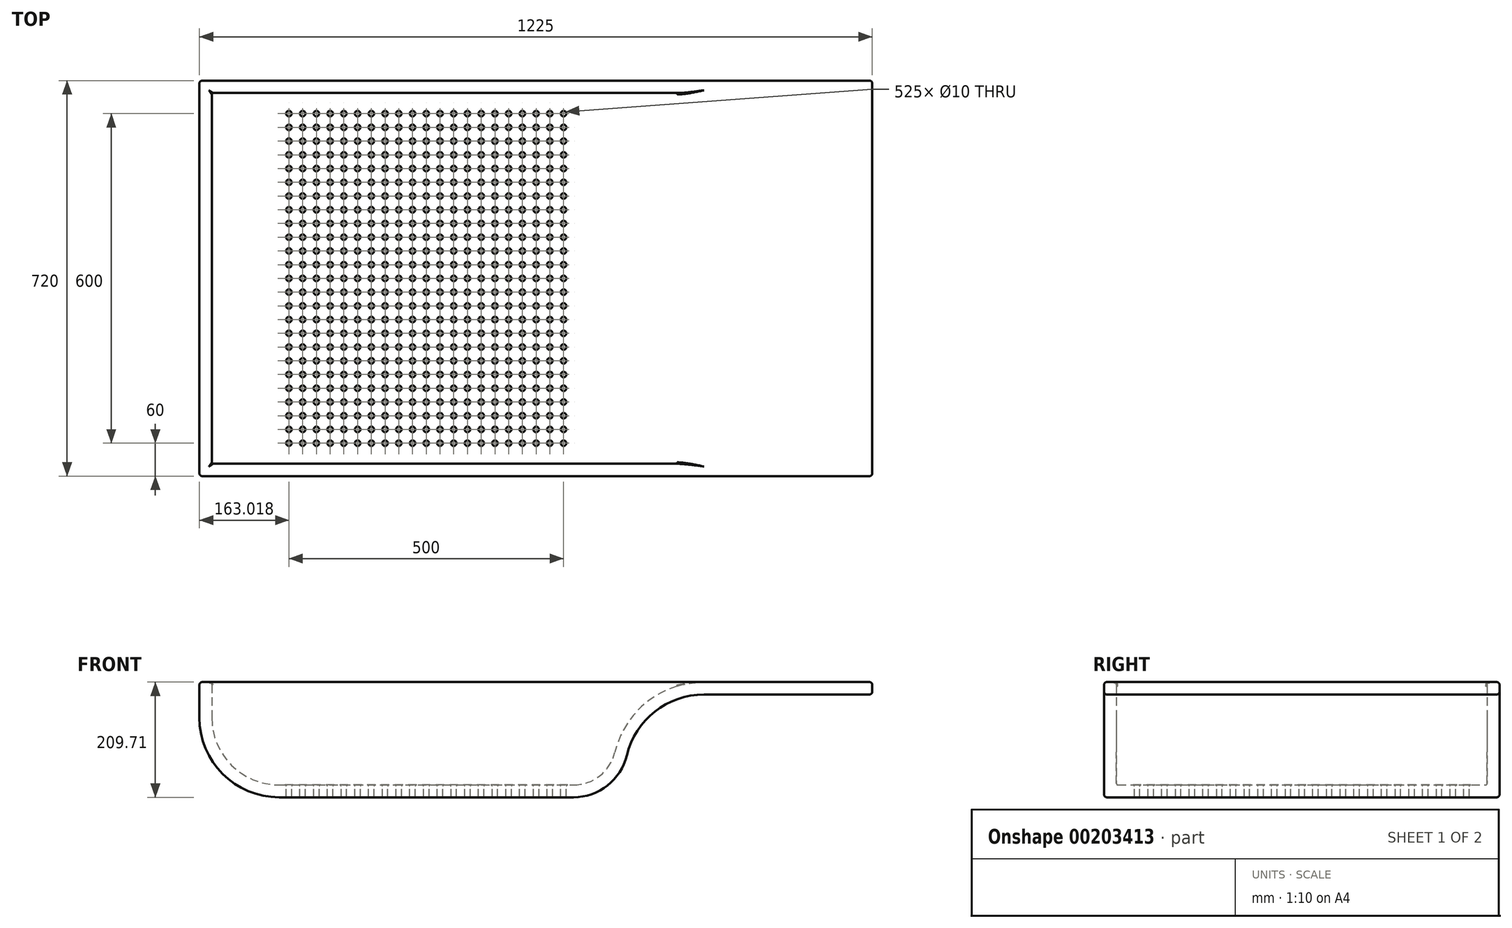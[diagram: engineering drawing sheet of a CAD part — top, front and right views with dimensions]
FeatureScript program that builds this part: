
annotation { "Feature Type Name" : "Feature", "Feature Type Description" : "" }
export const myFeature = defineFeature(function(context is Context, id is Id, definition is map)
    precondition{}
    {
        {
            var Q0;
            Q0=qCreatedBy(makeId("Front.planeOp"),FACE);
            var sketch = newSketch(context, id + "F0", { "sketchPlane" : qUnion([Q0])});
            skLineSegment(sketch, "E0.bottom", {"start": v(-612.5, 108.01) * mm, "end": v(612.5, 108.01) * mm});
            skLineSegment(sketch, "E0.top", {"start": v(-467.5, -101.7) * mm, "end": v(68.54, -101.7) * mm});
            skLineSegment(sketch, "E0.left", {"start": v(-612.5, 108.01) * mm, "end": v(-612.5, 43.3) * mm});
            skPoint(sketch, "E0.middle", {"position": v(0, 0) * mm});
            skPoint(sketch, "E1", {"position": v(207.5, -101.7) * mm});
            skPoint(sketch, "E2", {"position": v(207.5, 108.01) * mm});
            skPoint(sketch, "E3", {"position": v(612.5, 85.51) * mm});
            skLineSegment(sketch, "E4", {"start": v(306.28, 85.51) * mm, "end": v(612.5, 85.51) * mm});
            skArc(sketch, "E5.filletArc", {"start": v(-612.5, 43.3) * mm, "mid": v(-570.03, -59.23) * mm, "end": v(-467.5, -101.7) * mm});
            skArc(sketch, "E6", {"start": v(306.28, 85.51) * mm, "mid": v(216.84, 54.53) * mm, "end": v(165.75, -25.15) * mm});
            skArc(sketch, "E7.filletArc", {"start": v(68.54, -101.7) * mm, "mid": v(130.4, -80.27) * mm, "end": v(165.75, -25.15) * mm});
            skLineSegment(sketch, "E8", {"start": v(612.5, 108.01) * mm, "end": v(612.5, 85.51) * mm});
            skPoint(sketch, "E9", {"position": v(308.18, 108.01) * mm});
            skSolve(sketch);
        }
        {
            var Q0;
            Q0=qSketchRegion(id+"F0",true);
            extrude(context, id + "F1", {"entities" : qUnion([Q0]), "depth" : 360 * mm, "hasSecondDirection" : true, "secondDirectionOppositeDirection" : true, "secondDirectionDepth" : 360 * mm});
        }
        {
            var Q0;
            Q0=makeQuery(id+"F1.opExtrude","SWEPT_FACE",FACE,{"disambiguationData":[OSD([sQuery(id+"F0.wireOp",EDGE,"E0.bottom")])]});
            shell(context, id + "F2", {"entities" : qUnion([Q0]), "thickness" : 22.5 * mm});
        }
        {
            var Q0;
            Q0=makeQuery(id+"F1.opExtrude","CAP_EDGE",EDGE,{"disambiguationData":[OSD([sQuery(id+"F0.wireOp",EDGE,"E0.bottom")])],"isStart":false});
            var Q1;
            Q1=makeQuery(id+"F1.opExtrude","CAP_EDGE",EDGE,{"disambiguationData":[OSD([sQuery(id+"F0.wireOp",EDGE,"E8")])],"isStart":false});
            var Q2;
            Q2=makeQuery(id+"F1.opExtrude","SWEPT_EDGE",EDGE,{"disambiguationData":[OSD([sQuery(id+"F0.wireOp",EDGE,"E0.bottom"),sQuery(id+"F0.wireOp",EDGE,"E8")])]});
            var Q3;
            Q3=makeQuery(id+"F1.opExtrude","SWEPT_EDGE",EDGE,{"disambiguationData":[OSD([sQuery(id+"F0.wireOp",EDGE,"E4"),sQuery(id+"F0.wireOp",EDGE,"E8")])]});
            var Q4;
            Q4=makeQuery(id+"F1.opExtrude","CAP_EDGE",EDGE,{"disambiguationData":[OSD([sQuery(id+"F0.wireOp",EDGE,"E8")])],"isStart":true});
            var Q5;
            Q5=makeQuery(id+"F1.opExtrude","CAP_EDGE",EDGE,{"disambiguationData":[OSD([sQuery(id+"F0.wireOp",EDGE,"E4")])],"isStart":true});
            var Q6;
            Q6=makeQuery(id+"F1.opExtrude","CAP_EDGE",EDGE,{"disambiguationData":[OSD([sQuery(id+"F0.wireOp",EDGE,"E0.bottom")])],"isStart":true});
            var Q7;
            {var subQ0=sQuery(id+"F0.wireOp",EDGE,"E0.bottom");Q7=makeQuery(id+"F2.opShell","OFFSET_EDGE",EDGE,{"disambiguationData":[OSD([subQ0]),TDD([makeQuery(id+"F1.opExtrude","CAP_EDGE",EDGE,{"disambiguationData":[OSD([subQ0])],"isStart":true})])]});}
            var Q8;
            {var subQ0=sQuery(id+"F0.wireOp",EDGE,"E0.bottom");Q8=makeQuery(id+"F2.opShell","OFFSET_EDGE",EDGE,{"disambiguationData":[OSD([subQ0]),TDD([makeQuery(id+"F1.opExtrude","CAP_EDGE",EDGE,{"disambiguationData":[OSD([subQ0])],"isStart":false})])]});}
            var Q9;
            Q9=makeQuery(id+"F1.opExtrude","CAP_EDGE",EDGE,{"disambiguationData":[OSD([sQuery(id+"F0.wireOp",EDGE,"E6")])],"isStart":false});
            var Q10;
            Q10=makeQuery(id+"F2.opShell","OFFSET_EDGE",EDGE,{"disambiguationData":[OSD([sQuery(id+"F0.wireOp",EDGE,"E0.bottom"),sQuery(id+"F0.wireOp",EDGE,"E0.left")])]});
            var Q11;
            Q11=makeQuery(id+"F1.opExtrude","SWEPT_EDGE",EDGE,{"disambiguationData":[OSD([sQuery(id+"F0.wireOp",EDGE,"E0.bottom"),sQuery(id+"F0.wireOp",EDGE,"E0.left")])]});
            fillet(context, id + "F3", {"entities" : qUnion([Q0, Q1, Q2, Q3, Q4, Q5, Q6, Q7, Q8, Q9, Q10, Q11]), "radius" : 5 * mm, "tangentPropagation" : true, "allowEdgeOverflow" : false});
        }
        {
            var Q0;
            Q0=makeQuery(id+"F2.opShell","OFFSET_FACE",FACE,{"disambiguationData":[OSD([sQuery(id+"F0.wireOp",EDGE,"E0.top")])]});
            var sketch = newSketch(context, id + "F4", { "sketchPlane" : qUnion([Q0])});
            skCircle(sketch, "E10", {"center": v(-199.48, 0) * mm, "radius": 5 * mm});
            skPoint(sketch, "E10.centerSnap0", {"position": v(-199.48, 337.5) * mm});
            skCircle(sketch, "E11.0.1.0", {"center": v(-199.48, 25) * mm, "radius": 5 * mm});
            skCircle(sketch, "E11.0.2.0", {"center": v(-199.48, 50) * mm, "radius": 5 * mm});
            skCircle(sketch, "E11.0.3.0", {"center": v(-199.48, 75) * mm, "radius": 5 * mm});
            skCircle(sketch, "E11.0.4.0", {"center": v(-199.48, 100) * mm, "radius": 5 * mm});
            skCircle(sketch, "E11.0.5.0", {"center": v(-199.48, 125) * mm, "radius": 5 * mm});
            skCircle(sketch, "E11.0.6.0", {"center": v(-199.48, 150) * mm, "radius": 5 * mm});
            skCircle(sketch, "E11.0.7.0", {"center": v(-199.48, 175) * mm, "radius": 5 * mm});
            skCircle(sketch, "E11.0.8.0", {"center": v(-199.48, 200) * mm, "radius": 5 * mm});
            skCircle(sketch, "E11.0.9.0", {"center": v(-199.48, 225) * mm, "radius": 5 * mm});
            skCircle(sketch, "E11.0.10.0", {"center": v(-199.48, 250) * mm, "radius": 5 * mm});
            skCircle(sketch, "E11.0.11.0", {"center": v(-199.48, 275) * mm, "radius": 5 * mm});
            skCircle(sketch, "E11.0.12.0", {"center": v(-199.48, 300) * mm, "radius": 5 * mm});
            skCircle(sketch, "E11.1.0.0", {"center": v(-174.48, 0) * mm, "radius": 5 * mm});
            skCircle(sketch, "E11.1.1.0", {"center": v(-174.48, 25) * mm, "radius": 5 * mm});
            skCircle(sketch, "E11.1.2.0", {"center": v(-174.48, 50) * mm, "radius": 5 * mm});
            skCircle(sketch, "E11.1.3.0", {"center": v(-174.48, 75) * mm, "radius": 5 * mm});
            skCircle(sketch, "E11.1.4.0", {"center": v(-174.48, 100) * mm, "radius": 5 * mm});
            skCircle(sketch, "E11.1.5.0", {"center": v(-174.48, 125) * mm, "radius": 5 * mm});
            skCircle(sketch, "E11.1.6.0", {"center": v(-174.48, 150) * mm, "radius": 5 * mm});
            skCircle(sketch, "E11.1.7.0", {"center": v(-174.48, 175) * mm, "radius": 5 * mm});
            skCircle(sketch, "E11.1.8.0", {"center": v(-174.48, 200) * mm, "radius": 5 * mm});
            skCircle(sketch, "E11.1.9.0", {"center": v(-174.48, 225) * mm, "radius": 5 * mm});
            skCircle(sketch, "E11.1.10.0", {"center": v(-174.48, 250) * mm, "radius": 5 * mm});
            skCircle(sketch, "E11.1.11.0", {"center": v(-174.48, 275) * mm, "radius": 5 * mm});
            skCircle(sketch, "E11.1.12.0", {"center": v(-174.48, 300) * mm, "radius": 5 * mm});
            skCircle(sketch, "E11.2.0.0", {"center": v(-149.48, 0) * mm, "radius": 5 * mm});
            skCircle(sketch, "E11.2.1.0", {"center": v(-149.48, 25) * mm, "radius": 5 * mm});
            skCircle(sketch, "E11.2.2.0", {"center": v(-149.48, 50) * mm, "radius": 5 * mm});
            skCircle(sketch, "E11.2.3.0", {"center": v(-149.48, 75) * mm, "radius": 5 * mm});
            skCircle(sketch, "E11.2.4.0", {"center": v(-149.48, 100) * mm, "radius": 5 * mm});
            skCircle(sketch, "E11.2.5.0", {"center": v(-149.48, 125) * mm, "radius": 5 * mm});
            skCircle(sketch, "E11.2.6.0", {"center": v(-149.48, 150) * mm, "radius": 5 * mm});
            skCircle(sketch, "E11.2.7.0", {"center": v(-149.48, 175) * mm, "radius": 5 * mm});
            skCircle(sketch, "E11.2.8.0", {"center": v(-149.48, 200) * mm, "radius": 5 * mm});
            skCircle(sketch, "E11.2.9.0", {"center": v(-149.48, 225) * mm, "radius": 5 * mm});
            skCircle(sketch, "E11.2.10.0", {"center": v(-149.48, 250) * mm, "radius": 5 * mm});
            skCircle(sketch, "E11.2.11.0", {"center": v(-149.48, 275) * mm, "radius": 5 * mm});
            skCircle(sketch, "E11.2.12.0", {"center": v(-149.48, 300) * mm, "radius": 5 * mm});
            skCircle(sketch, "E11.3.0.0", {"center": v(-124.48, 0) * mm, "radius": 5 * mm});
            skCircle(sketch, "E11.3.1.0", {"center": v(-124.48, 25) * mm, "radius": 5 * mm});
            skCircle(sketch, "E11.3.2.0", {"center": v(-124.48, 50) * mm, "radius": 5 * mm});
            skCircle(sketch, "E11.3.3.0", {"center": v(-124.48, 75) * mm, "radius": 5 * mm});
            skCircle(sketch, "E11.3.4.0", {"center": v(-124.48, 100) * mm, "radius": 5 * mm});
            skCircle(sketch, "E11.3.5.0", {"center": v(-124.48, 125) * mm, "radius": 5 * mm});
            skCircle(sketch, "E11.3.6.0", {"center": v(-124.48, 150) * mm, "radius": 5 * mm});
            skCircle(sketch, "E11.3.7.0", {"center": v(-124.48, 175) * mm, "radius": 5 * mm});
            skCircle(sketch, "E11.3.8.0", {"center": v(-124.48, 200) * mm, "radius": 5 * mm});
            skCircle(sketch, "E11.3.9.0", {"center": v(-124.48, 225) * mm, "radius": 5 * mm});
            skCircle(sketch, "E11.3.10.0", {"center": v(-124.48, 250) * mm, "radius": 5 * mm});
            skCircle(sketch, "E11.3.11.0", {"center": v(-124.48, 275) * mm, "radius": 5 * mm});
            skCircle(sketch, "E11.3.12.0", {"center": v(-124.48, 300) * mm, "radius": 5 * mm});
            skCircle(sketch, "E11.4.0.0", {"center": v(-99.48, 0) * mm, "radius": 5 * mm});
            skCircle(sketch, "E11.4.1.0", {"center": v(-99.48, 25) * mm, "radius": 5 * mm});
            skCircle(sketch, "E11.4.2.0", {"center": v(-99.48, 50) * mm, "radius": 5 * mm});
            skCircle(sketch, "E11.4.3.0", {"center": v(-99.48, 75) * mm, "radius": 5 * mm});
            skCircle(sketch, "E11.4.4.0", {"center": v(-99.48, 100) * mm, "radius": 5 * mm});
            skCircle(sketch, "E11.4.5.0", {"center": v(-99.48, 125) * mm, "radius": 5 * mm});
            skCircle(sketch, "E11.4.6.0", {"center": v(-99.48, 150) * mm, "radius": 5 * mm});
            skCircle(sketch, "E11.4.7.0", {"center": v(-99.48, 175) * mm, "radius": 5 * mm});
            skCircle(sketch, "E11.4.8.0", {"center": v(-99.48, 200) * mm, "radius": 5 * mm});
            skCircle(sketch, "E11.4.9.0", {"center": v(-99.48, 225) * mm, "radius": 5 * mm});
            skCircle(sketch, "E11.4.10.0", {"center": v(-99.48, 250) * mm, "radius": 5 * mm});
            skCircle(sketch, "E11.4.11.0", {"center": v(-99.48, 275) * mm, "radius": 5 * mm});
            skCircle(sketch, "E11.4.12.0", {"center": v(-99.48, 300) * mm, "radius": 5 * mm});
            skCircle(sketch, "E11.5.0.0", {"center": v(-74.48, 0) * mm, "radius": 5 * mm});
            skCircle(sketch, "E11.5.1.0", {"center": v(-74.48, 25) * mm, "radius": 5 * mm});
            skCircle(sketch, "E11.5.2.0", {"center": v(-74.48, 50) * mm, "radius": 5 * mm});
            skCircle(sketch, "E11.5.3.0", {"center": v(-74.48, 75) * mm, "radius": 5 * mm});
            skCircle(sketch, "E11.5.4.0", {"center": v(-74.48, 100) * mm, "radius": 5 * mm});
            skCircle(sketch, "E11.5.5.0", {"center": v(-74.48, 125) * mm, "radius": 5 * mm});
            skCircle(sketch, "E11.5.6.0", {"center": v(-74.48, 150) * mm, "radius": 5 * mm});
            skCircle(sketch, "E11.5.7.0", {"center": v(-74.48, 175) * mm, "radius": 5 * mm});
            skCircle(sketch, "E11.5.8.0", {"center": v(-74.48, 200) * mm, "radius": 5 * mm});
            skCircle(sketch, "E11.5.9.0", {"center": v(-74.48, 225) * mm, "radius": 5 * mm});
            skCircle(sketch, "E11.5.10.0", {"center": v(-74.48, 250) * mm, "radius": 5 * mm});
            skCircle(sketch, "E11.5.11.0", {"center": v(-74.48, 275) * mm, "radius": 5 * mm});
            skCircle(sketch, "E11.5.12.0", {"center": v(-74.48, 300) * mm, "radius": 5 * mm});
            skCircle(sketch, "E11.6.0.0", {"center": v(-49.48, 0) * mm, "radius": 5 * mm});
            skCircle(sketch, "E11.6.1.0", {"center": v(-49.48, 25) * mm, "radius": 5 * mm});
            skCircle(sketch, "E11.6.2.0", {"center": v(-49.48, 50) * mm, "radius": 5 * mm});
            skCircle(sketch, "E11.6.3.0", {"center": v(-49.48, 75) * mm, "radius": 5 * mm});
            skCircle(sketch, "E11.6.4.0", {"center": v(-49.48, 100) * mm, "radius": 5 * mm});
            skCircle(sketch, "E11.6.5.0", {"center": v(-49.48, 125) * mm, "radius": 5 * mm});
            skCircle(sketch, "E11.6.6.0", {"center": v(-49.48, 150) * mm, "radius": 5 * mm});
            skCircle(sketch, "E11.6.7.0", {"center": v(-49.48, 175) * mm, "radius": 5 * mm});
            skCircle(sketch, "E11.6.8.0", {"center": v(-49.48, 200) * mm, "radius": 5 * mm});
            skCircle(sketch, "E11.6.9.0", {"center": v(-49.48, 225) * mm, "radius": 5 * mm});
            skCircle(sketch, "E11.6.10.0", {"center": v(-49.48, 250) * mm, "radius": 5 * mm});
            skCircle(sketch, "E11.6.11.0", {"center": v(-49.48, 275) * mm, "radius": 5 * mm});
            skCircle(sketch, "E11.6.12.0", {"center": v(-49.48, 300) * mm, "radius": 5 * mm});
            skCircle(sketch, "E11.7.0.0", {"center": v(-24.48, 0) * mm, "radius": 5 * mm});
            skCircle(sketch, "E11.7.1.0", {"center": v(-24.48, 25) * mm, "radius": 5 * mm});
            skCircle(sketch, "E11.7.2.0", {"center": v(-24.48, 50) * mm, "radius": 5 * mm});
            skCircle(sketch, "E11.7.3.0", {"center": v(-24.48, 75) * mm, "radius": 5 * mm});
            skCircle(sketch, "E11.7.4.0", {"center": v(-24.48, 100) * mm, "radius": 5 * mm});
            skCircle(sketch, "E11.7.5.0", {"center": v(-24.48, 125) * mm, "radius": 5 * mm});
            skCircle(sketch, "E11.7.6.0", {"center": v(-24.48, 150) * mm, "radius": 5 * mm});
            skCircle(sketch, "E11.7.7.0", {"center": v(-24.48, 175) * mm, "radius": 5 * mm});
            skCircle(sketch, "E11.7.8.0", {"center": v(-24.48, 200) * mm, "radius": 5 * mm});
            skCircle(sketch, "E11.7.9.0", {"center": v(-24.48, 225) * mm, "radius": 5 * mm});
            skCircle(sketch, "E11.7.10.0", {"center": v(-24.48, 250) * mm, "radius": 5 * mm});
            skCircle(sketch, "E11.7.11.0", {"center": v(-24.48, 275) * mm, "radius": 5 * mm});
            skCircle(sketch, "E11.7.12.0", {"center": v(-24.48, 300) * mm, "radius": 5 * mm});
            skCircle(sketch, "E11.8.0.0", {"center": v(0.52, 0) * mm, "radius": 5 * mm});
            skCircle(sketch, "E11.8.1.0", {"center": v(0.52, 25) * mm, "radius": 5 * mm});
            skCircle(sketch, "E11.8.2.0", {"center": v(0.52, 50) * mm, "radius": 5 * mm});
            skCircle(sketch, "E11.8.3.0", {"center": v(0.52, 75) * mm, "radius": 5 * mm});
            skCircle(sketch, "E11.8.4.0", {"center": v(0.52, 100) * mm, "radius": 5 * mm});
            skCircle(sketch, "E11.8.5.0", {"center": v(0.52, 125) * mm, "radius": 5 * mm});
            skCircle(sketch, "E11.8.6.0", {"center": v(0.52, 150) * mm, "radius": 5 * mm});
            skCircle(sketch, "E11.8.7.0", {"center": v(0.52, 175) * mm, "radius": 5 * mm});
            skCircle(sketch, "E11.8.8.0", {"center": v(0.52, 200) * mm, "radius": 5 * mm});
            skCircle(sketch, "E11.8.9.0", {"center": v(0.52, 225) * mm, "radius": 5 * mm});
            skCircle(sketch, "E11.8.10.0", {"center": v(0.52, 250) * mm, "radius": 5 * mm});
            skCircle(sketch, "E11.8.11.0", {"center": v(0.52, 275) * mm, "radius": 5 * mm});
            skCircle(sketch, "E11.8.12.0", {"center": v(0.52, 300) * mm, "radius": 5 * mm});
            skCircle(sketch, "E11.9.0.0", {"center": v(25.52, 0) * mm, "radius": 5 * mm});
            skCircle(sketch, "E11.9.1.0", {"center": v(25.52, 25) * mm, "radius": 5 * mm});
            skCircle(sketch, "E11.9.2.0", {"center": v(25.52, 50) * mm, "radius": 5 * mm});
            skCircle(sketch, "E11.9.3.0", {"center": v(25.52, 75) * mm, "radius": 5 * mm});
            skCircle(sketch, "E11.9.4.0", {"center": v(25.52, 100) * mm, "radius": 5 * mm});
            skCircle(sketch, "E11.9.5.0", {"center": v(25.52, 125) * mm, "radius": 5 * mm});
            skCircle(sketch, "E11.9.6.0", {"center": v(25.52, 150) * mm, "radius": 5 * mm});
            skCircle(sketch, "E11.9.7.0", {"center": v(25.52, 175) * mm, "radius": 5 * mm});
            skCircle(sketch, "E11.9.8.0", {"center": v(25.52, 200) * mm, "radius": 5 * mm});
            skCircle(sketch, "E11.9.9.0", {"center": v(25.52, 225) * mm, "radius": 5 * mm});
            skCircle(sketch, "E11.9.10.0", {"center": v(25.52, 250) * mm, "radius": 5 * mm});
            skCircle(sketch, "E11.9.11.0", {"center": v(25.52, 275) * mm, "radius": 5 * mm});
            skCircle(sketch, "E11.9.12.0", {"center": v(25.52, 300) * mm, "radius": 5 * mm});
            skCircle(sketch, "E11.10.0.0", {"center": v(50.52, 0) * mm, "radius": 5 * mm});
            skCircle(sketch, "E11.10.1.0", {"center": v(50.52, 25) * mm, "radius": 5 * mm});
            skCircle(sketch, "E11.10.2.0", {"center": v(50.52, 50) * mm, "radius": 5 * mm});
            skCircle(sketch, "E11.10.3.0", {"center": v(50.52, 75) * mm, "radius": 5 * mm});
            skCircle(sketch, "E11.10.4.0", {"center": v(50.52, 100) * mm, "radius": 5 * mm});
            skCircle(sketch, "E11.10.5.0", {"center": v(50.52, 125) * mm, "radius": 5 * mm});
            skCircle(sketch, "E11.10.6.0", {"center": v(50.52, 150) * mm, "radius": 5 * mm});
            skCircle(sketch, "E11.10.7.0", {"center": v(50.52, 175) * mm, "radius": 5 * mm});
            skCircle(sketch, "E11.10.8.0", {"center": v(50.52, 200) * mm, "radius": 5 * mm});
            skCircle(sketch, "E11.10.9.0", {"center": v(50.52, 225) * mm, "radius": 5 * mm});
            skCircle(sketch, "E11.10.10.0", {"center": v(50.52, 250) * mm, "radius": 5 * mm});
            skCircle(sketch, "E11.10.11.0", {"center": v(50.52, 275) * mm, "radius": 5 * mm});
            skCircle(sketch, "E11.10.12.0", {"center": v(50.52, 300) * mm, "radius": 5 * mm});
            skCircle(sketch, "E12.0.1.0", {"center": v(-199.48, -25) * mm, "radius": 5 * mm});
            skCircle(sketch, "E12.0.2.0", {"center": v(-199.48, -50) * mm, "radius": 5 * mm});
            skCircle(sketch, "E12.0.3.0", {"center": v(-199.48, -75) * mm, "radius": 5 * mm});
            skCircle(sketch, "E12.0.4.0", {"center": v(-199.48, -100) * mm, "radius": 5 * mm});
            skCircle(sketch, "E12.0.5.0", {"center": v(-199.48, -125) * mm, "radius": 5 * mm});
            skCircle(sketch, "E12.0.6.0", {"center": v(-199.48, -150) * mm, "radius": 5 * mm});
            skCircle(sketch, "E12.0.7.0", {"center": v(-199.48, -175) * mm, "radius": 5 * mm});
            skCircle(sketch, "E12.0.8.0", {"center": v(-199.48, -200) * mm, "radius": 5 * mm});
            skCircle(sketch, "E12.0.9.0", {"center": v(-199.48, -225) * mm, "radius": 5 * mm});
            skCircle(sketch, "E12.0.10.0", {"center": v(-199.48, -250) * mm, "radius": 5 * mm});
            skCircle(sketch, "E12.0.11.0", {"center": v(-199.48, -275) * mm, "radius": 5 * mm});
            skCircle(sketch, "E12.0.12.0", {"center": v(-199.48, -300) * mm, "radius": 5 * mm});
            skCircle(sketch, "E12.1.1.0", {"center": v(-174.48, -25) * mm, "radius": 5 * mm});
            skCircle(sketch, "E12.1.2.0", {"center": v(-174.48, -50) * mm, "radius": 5 * mm});
            skCircle(sketch, "E12.1.3.0", {"center": v(-174.48, -75) * mm, "radius": 5 * mm});
            skCircle(sketch, "E12.1.4.0", {"center": v(-174.48, -100) * mm, "radius": 5 * mm});
            skCircle(sketch, "E12.1.5.0", {"center": v(-174.48, -125) * mm, "radius": 5 * mm});
            skCircle(sketch, "E12.1.6.0", {"center": v(-174.48, -150) * mm, "radius": 5 * mm});
            skCircle(sketch, "E12.1.7.0", {"center": v(-174.48, -175) * mm, "radius": 5 * mm});
            skCircle(sketch, "E12.1.8.0", {"center": v(-174.48, -200) * mm, "radius": 5 * mm});
            skCircle(sketch, "E12.1.9.0", {"center": v(-174.48, -225) * mm, "radius": 5 * mm});
            skCircle(sketch, "E12.1.10.0", {"center": v(-174.48, -250) * mm, "radius": 5 * mm});
            skCircle(sketch, "E12.1.11.0", {"center": v(-174.48, -275) * mm, "radius": 5 * mm});
            skCircle(sketch, "E12.1.12.0", {"center": v(-174.48, -300) * mm, "radius": 5 * mm});
            skCircle(sketch, "E12.2.1.0", {"center": v(-149.48, -25) * mm, "radius": 5 * mm});
            skCircle(sketch, "E12.2.2.0", {"center": v(-149.48, -50) * mm, "radius": 5 * mm});
            skCircle(sketch, "E12.2.3.0", {"center": v(-149.48, -75) * mm, "radius": 5 * mm});
            skCircle(sketch, "E12.2.4.0", {"center": v(-149.48, -100) * mm, "radius": 5 * mm});
            skCircle(sketch, "E12.2.5.0", {"center": v(-149.48, -125) * mm, "radius": 5 * mm});
            skCircle(sketch, "E12.2.6.0", {"center": v(-149.48, -150) * mm, "radius": 5 * mm});
            skCircle(sketch, "E12.2.7.0", {"center": v(-149.48, -175) * mm, "radius": 5 * mm});
            skCircle(sketch, "E12.2.8.0", {"center": v(-149.48, -200) * mm, "radius": 5 * mm});
            skCircle(sketch, "E12.2.9.0", {"center": v(-149.48, -225) * mm, "radius": 5 * mm});
            skCircle(sketch, "E12.2.10.0", {"center": v(-149.48, -250) * mm, "radius": 5 * mm});
            skCircle(sketch, "E12.2.11.0", {"center": v(-149.48, -275) * mm, "radius": 5 * mm});
            skCircle(sketch, "E12.2.12.0", {"center": v(-149.48, -300) * mm, "radius": 5 * mm});
            skCircle(sketch, "E12.3.1.0", {"center": v(-124.48, -25) * mm, "radius": 5 * mm});
            skCircle(sketch, "E12.3.2.0", {"center": v(-124.48, -50) * mm, "radius": 5 * mm});
            skCircle(sketch, "E12.3.3.0", {"center": v(-124.48, -75) * mm, "radius": 5 * mm});
            skCircle(sketch, "E12.3.4.0", {"center": v(-124.48, -100) * mm, "radius": 5 * mm});
            skCircle(sketch, "E12.3.5.0", {"center": v(-124.48, -125) * mm, "radius": 5 * mm});
            skCircle(sketch, "E12.3.6.0", {"center": v(-124.48, -150) * mm, "radius": 5 * mm});
            skCircle(sketch, "E12.3.7.0", {"center": v(-124.48, -175) * mm, "radius": 5 * mm});
            skCircle(sketch, "E12.3.8.0", {"center": v(-124.48, -200) * mm, "radius": 5 * mm});
            skCircle(sketch, "E12.3.9.0", {"center": v(-124.48, -225) * mm, "radius": 5 * mm});
            skCircle(sketch, "E12.3.10.0", {"center": v(-124.48, -250) * mm, "radius": 5 * mm});
            skCircle(sketch, "E12.3.11.0", {"center": v(-124.48, -275) * mm, "radius": 5 * mm});
            skCircle(sketch, "E12.3.12.0", {"center": v(-124.48, -300) * mm, "radius": 5 * mm});
            skCircle(sketch, "E12.4.1.0", {"center": v(-99.48, -25) * mm, "radius": 5 * mm});
            skCircle(sketch, "E12.4.2.0", {"center": v(-99.48, -50) * mm, "radius": 5 * mm});
            skCircle(sketch, "E12.4.3.0", {"center": v(-99.48, -75) * mm, "radius": 5 * mm});
            skCircle(sketch, "E12.4.4.0", {"center": v(-99.48, -100) * mm, "radius": 5 * mm});
            skCircle(sketch, "E12.4.5.0", {"center": v(-99.48, -125) * mm, "radius": 5 * mm});
            skCircle(sketch, "E12.4.6.0", {"center": v(-99.48, -150) * mm, "radius": 5 * mm});
            skCircle(sketch, "E12.4.7.0", {"center": v(-99.48, -175) * mm, "radius": 5 * mm});
            skCircle(sketch, "E12.4.8.0", {"center": v(-99.48, -200) * mm, "radius": 5 * mm});
            skCircle(sketch, "E12.4.9.0", {"center": v(-99.48, -225) * mm, "radius": 5 * mm});
            skCircle(sketch, "E12.4.10.0", {"center": v(-99.48, -250) * mm, "radius": 5 * mm});
            skCircle(sketch, "E12.4.11.0", {"center": v(-99.48, -275) * mm, "radius": 5 * mm});
            skCircle(sketch, "E12.4.12.0", {"center": v(-99.48, -300) * mm, "radius": 5 * mm});
            skCircle(sketch, "E12.5.1.0", {"center": v(-74.48, -25) * mm, "radius": 5 * mm});
            skCircle(sketch, "E12.5.2.0", {"center": v(-74.48, -50) * mm, "radius": 5 * mm});
            skCircle(sketch, "E12.5.3.0", {"center": v(-74.48, -75) * mm, "radius": 5 * mm});
            skCircle(sketch, "E12.5.4.0", {"center": v(-74.48, -100) * mm, "radius": 5 * mm});
            skCircle(sketch, "E12.5.5.0", {"center": v(-74.48, -125) * mm, "radius": 5 * mm});
            skCircle(sketch, "E12.5.6.0", {"center": v(-74.48, -150) * mm, "radius": 5 * mm});
            skCircle(sketch, "E12.5.7.0", {"center": v(-74.48, -175) * mm, "radius": 5 * mm});
            skCircle(sketch, "E12.5.8.0", {"center": v(-74.48, -200) * mm, "radius": 5 * mm});
            skCircle(sketch, "E12.5.9.0", {"center": v(-74.48, -225) * mm, "radius": 5 * mm});
            skCircle(sketch, "E12.5.10.0", {"center": v(-74.48, -250) * mm, "radius": 5 * mm});
            skCircle(sketch, "E12.5.11.0", {"center": v(-74.48, -275) * mm, "radius": 5 * mm});
            skCircle(sketch, "E12.5.12.0", {"center": v(-74.48, -300) * mm, "radius": 5 * mm});
            skCircle(sketch, "E12.6.1.0", {"center": v(-49.48, -25) * mm, "radius": 5 * mm});
            skCircle(sketch, "E12.6.2.0", {"center": v(-49.48, -50) * mm, "radius": 5 * mm});
            skCircle(sketch, "E12.6.3.0", {"center": v(-49.48, -75) * mm, "radius": 5 * mm});
            skCircle(sketch, "E12.6.4.0", {"center": v(-49.48, -100) * mm, "radius": 5 * mm});
            skCircle(sketch, "E12.6.5.0", {"center": v(-49.48, -125) * mm, "radius": 5 * mm});
            skCircle(sketch, "E12.6.6.0", {"center": v(-49.48, -150) * mm, "radius": 5 * mm});
            skCircle(sketch, "E12.6.7.0", {"center": v(-49.48, -175) * mm, "radius": 5 * mm});
            skCircle(sketch, "E12.6.8.0", {"center": v(-49.48, -200) * mm, "radius": 5 * mm});
            skCircle(sketch, "E12.6.9.0", {"center": v(-49.48, -225) * mm, "radius": 5 * mm});
            skCircle(sketch, "E12.6.10.0", {"center": v(-49.48, -250) * mm, "radius": 5 * mm});
            skCircle(sketch, "E12.6.11.0", {"center": v(-49.48, -275) * mm, "radius": 5 * mm});
            skCircle(sketch, "E12.6.12.0", {"center": v(-49.48, -300) * mm, "radius": 5 * mm});
            skCircle(sketch, "E12.7.1.0", {"center": v(-24.48, -25) * mm, "radius": 5 * mm});
            skCircle(sketch, "E12.7.2.0", {"center": v(-24.48, -50) * mm, "radius": 5 * mm});
            skCircle(sketch, "E12.7.3.0", {"center": v(-24.48, -75) * mm, "radius": 5 * mm});
            skCircle(sketch, "E12.7.4.0", {"center": v(-24.48, -100) * mm, "radius": 5 * mm});
            skCircle(sketch, "E12.7.5.0", {"center": v(-24.48, -125) * mm, "radius": 5 * mm});
            skCircle(sketch, "E12.7.6.0", {"center": v(-24.48, -150) * mm, "radius": 5 * mm});
            skCircle(sketch, "E12.7.7.0", {"center": v(-24.48, -175) * mm, "radius": 5 * mm});
            skCircle(sketch, "E12.7.8.0", {"center": v(-24.48, -200) * mm, "radius": 5 * mm});
            skCircle(sketch, "E12.7.9.0", {"center": v(-24.48, -225) * mm, "radius": 5 * mm});
            skCircle(sketch, "E12.7.10.0", {"center": v(-24.48, -250) * mm, "radius": 5 * mm});
            skCircle(sketch, "E12.7.11.0", {"center": v(-24.48, -275) * mm, "radius": 5 * mm});
            skCircle(sketch, "E12.7.12.0", {"center": v(-24.48, -300) * mm, "radius": 5 * mm});
            skCircle(sketch, "E12.8.1.0", {"center": v(0.52, -25) * mm, "radius": 5 * mm});
            skCircle(sketch, "E12.8.2.0", {"center": v(0.52, -50) * mm, "radius": 5 * mm});
            skCircle(sketch, "E12.8.3.0", {"center": v(0.52, -75) * mm, "radius": 5 * mm});
            skCircle(sketch, "E12.8.4.0", {"center": v(0.52, -100) * mm, "radius": 5 * mm});
            skCircle(sketch, "E12.8.5.0", {"center": v(0.52, -125) * mm, "radius": 5 * mm});
            skCircle(sketch, "E12.8.6.0", {"center": v(0.52, -150) * mm, "radius": 5 * mm});
            skCircle(sketch, "E12.8.7.0", {"center": v(0.52, -175) * mm, "radius": 5 * mm});
            skCircle(sketch, "E12.8.8.0", {"center": v(0.52, -200) * mm, "radius": 5 * mm});
            skCircle(sketch, "E12.8.9.0", {"center": v(0.52, -225) * mm, "radius": 5 * mm});
            skCircle(sketch, "E12.8.10.0", {"center": v(0.52, -250) * mm, "radius": 5 * mm});
            skCircle(sketch, "E12.8.11.0", {"center": v(0.52, -275) * mm, "radius": 5 * mm});
            skCircle(sketch, "E12.8.12.0", {"center": v(0.52, -300) * mm, "radius": 5 * mm});
            skCircle(sketch, "E12.9.1.0", {"center": v(25.52, -25) * mm, "radius": 5 * mm});
            skCircle(sketch, "E12.9.2.0", {"center": v(25.52, -50) * mm, "radius": 5 * mm});
            skCircle(sketch, "E12.9.3.0", {"center": v(25.52, -75) * mm, "radius": 5 * mm});
            skCircle(sketch, "E12.9.4.0", {"center": v(25.52, -100) * mm, "radius": 5 * mm});
            skCircle(sketch, "E12.9.5.0", {"center": v(25.52, -125) * mm, "radius": 5 * mm});
            skCircle(sketch, "E12.9.6.0", {"center": v(25.52, -150) * mm, "radius": 5 * mm});
            skCircle(sketch, "E12.9.7.0", {"center": v(25.52, -175) * mm, "radius": 5 * mm});
            skCircle(sketch, "E12.9.8.0", {"center": v(25.52, -200) * mm, "radius": 5 * mm});
            skCircle(sketch, "E12.9.9.0", {"center": v(25.52, -225) * mm, "radius": 5 * mm});
            skCircle(sketch, "E12.9.10.0", {"center": v(25.52, -250) * mm, "radius": 5 * mm});
            skCircle(sketch, "E12.9.11.0", {"center": v(25.52, -275) * mm, "radius": 5 * mm});
            skCircle(sketch, "E12.9.12.0", {"center": v(25.52, -300) * mm, "radius": 5 * mm});
            skCircle(sketch, "E12.10.1.0", {"center": v(50.52, -25) * mm, "radius": 5 * mm});
            skCircle(sketch, "E12.10.2.0", {"center": v(50.52, -50) * mm, "radius": 5 * mm});
            skCircle(sketch, "E12.10.3.0", {"center": v(50.52, -75) * mm, "radius": 5 * mm});
            skCircle(sketch, "E12.10.4.0", {"center": v(50.52, -100) * mm, "radius": 5 * mm});
            skCircle(sketch, "E12.10.5.0", {"center": v(50.52, -125) * mm, "radius": 5 * mm});
            skCircle(sketch, "E12.10.6.0", {"center": v(50.52, -150) * mm, "radius": 5 * mm});
            skCircle(sketch, "E12.10.7.0", {"center": v(50.52, -175) * mm, "radius": 5 * mm});
            skCircle(sketch, "E12.10.8.0", {"center": v(50.52, -200) * mm, "radius": 5 * mm});
            skCircle(sketch, "E12.10.9.0", {"center": v(50.52, -225) * mm, "radius": 5 * mm});
            skCircle(sketch, "E12.10.10.0", {"center": v(50.52, -250) * mm, "radius": 5 * mm});
            skCircle(sketch, "E12.10.11.0", {"center": v(50.52, -275) * mm, "radius": 5 * mm});
            skCircle(sketch, "E12.10.12.0", {"center": v(50.52, -300) * mm, "radius": 5 * mm});
            skCircle(sketch, "E13.1.0.0", {"center": v(-224.48, -300) * mm, "radius": 5 * mm});
            skCircle(sketch, "E13.1.1.0", {"center": v(-224.48, -275) * mm, "radius": 5 * mm});
            skCircle(sketch, "E13.1.2.0", {"center": v(-224.48, -250) * mm, "radius": 5 * mm});
            skCircle(sketch, "E13.1.3.0", {"center": v(-224.48, -225) * mm, "radius": 5 * mm});
            skCircle(sketch, "E13.1.4.0", {"center": v(-224.48, -200) * mm, "radius": 5 * mm});
            skCircle(sketch, "E13.1.5.0", {"center": v(-224.48, -175) * mm, "radius": 5 * mm});
            skCircle(sketch, "E13.1.6.0", {"center": v(-224.48, -150) * mm, "radius": 5 * mm});
            skCircle(sketch, "E13.1.7.0", {"center": v(-224.48, -125) * mm, "radius": 5 * mm});
            skCircle(sketch, "E13.1.8.0", {"center": v(-224.48, -100) * mm, "radius": 5 * mm});
            skCircle(sketch, "E13.1.9.0", {"center": v(-224.48, -75) * mm, "radius": 5 * mm});
            skCircle(sketch, "E13.1.10.0", {"center": v(-224.48, -50) * mm, "radius": 5 * mm});
            skCircle(sketch, "E13.1.11.0", {"center": v(-224.48, -25) * mm, "radius": 5 * mm});
            skCircle(sketch, "E13.1.12.0", {"center": v(-224.48, 0) * mm, "radius": 5 * mm});
            skCircle(sketch, "E13.1.13.0", {"center": v(-224.48, 25) * mm, "radius": 5 * mm});
            skCircle(sketch, "E13.1.14.0", {"center": v(-224.48, 50) * mm, "radius": 5 * mm});
            skCircle(sketch, "E13.1.15.0", {"center": v(-224.48, 75) * mm, "radius": 5 * mm});
            skCircle(sketch, "E13.1.16.0", {"center": v(-224.48, 100) * mm, "radius": 5 * mm});
            skCircle(sketch, "E13.1.17.0", {"center": v(-224.48, 125) * mm, "radius": 5 * mm});
            skCircle(sketch, "E13.1.18.0", {"center": v(-224.48, 150) * mm, "radius": 5 * mm});
            skCircle(sketch, "E13.1.19.0", {"center": v(-224.48, 175) * mm, "radius": 5 * mm});
            skCircle(sketch, "E13.1.20.0", {"center": v(-224.48, 200) * mm, "radius": 5 * mm});
            skCircle(sketch, "E13.1.21.0", {"center": v(-224.48, 225) * mm, "radius": 5 * mm});
            skCircle(sketch, "E13.1.22.0", {"center": v(-224.48, 250) * mm, "radius": 5 * mm});
            skCircle(sketch, "E13.1.23.0", {"center": v(-224.48, 275) * mm, "radius": 5 * mm});
            skCircle(sketch, "E13.1.24.0", {"center": v(-224.48, 300) * mm, "radius": 5 * mm});
            skCircle(sketch, "E13.2.0.0", {"center": v(-249.48, -300) * mm, "radius": 5 * mm});
            skCircle(sketch, "E13.2.1.0", {"center": v(-249.48, -275) * mm, "radius": 5 * mm});
            skCircle(sketch, "E13.2.2.0", {"center": v(-249.48, -250) * mm, "radius": 5 * mm});
            skCircle(sketch, "E13.2.3.0", {"center": v(-249.48, -225) * mm, "radius": 5 * mm});
            skCircle(sketch, "E13.2.4.0", {"center": v(-249.48, -200) * mm, "radius": 5 * mm});
            skCircle(sketch, "E13.2.5.0", {"center": v(-249.48, -175) * mm, "radius": 5 * mm});
            skCircle(sketch, "E13.2.6.0", {"center": v(-249.48, -150) * mm, "radius": 5 * mm});
            skCircle(sketch, "E13.2.7.0", {"center": v(-249.48, -125) * mm, "radius": 5 * mm});
            skCircle(sketch, "E13.2.8.0", {"center": v(-249.48, -100) * mm, "radius": 5 * mm});
            skCircle(sketch, "E13.2.9.0", {"center": v(-249.48, -75) * mm, "radius": 5 * mm});
            skCircle(sketch, "E13.2.10.0", {"center": v(-249.48, -50) * mm, "radius": 5 * mm});
            skCircle(sketch, "E13.2.11.0", {"center": v(-249.48, -25) * mm, "radius": 5 * mm});
            skCircle(sketch, "E13.2.12.0", {"center": v(-249.48, 0) * mm, "radius": 5 * mm});
            skCircle(sketch, "E13.2.13.0", {"center": v(-249.48, 25) * mm, "radius": 5 * mm});
            skCircle(sketch, "E13.2.14.0", {"center": v(-249.48, 50) * mm, "radius": 5 * mm});
            skCircle(sketch, "E13.2.15.0", {"center": v(-249.48, 75) * mm, "radius": 5 * mm});
            skCircle(sketch, "E13.2.16.0", {"center": v(-249.48, 100) * mm, "radius": 5 * mm});
            skCircle(sketch, "E13.2.17.0", {"center": v(-249.48, 125) * mm, "radius": 5 * mm});
            skCircle(sketch, "E13.2.18.0", {"center": v(-249.48, 150) * mm, "radius": 5 * mm});
            skCircle(sketch, "E13.2.19.0", {"center": v(-249.48, 175) * mm, "radius": 5 * mm});
            skCircle(sketch, "E13.2.20.0", {"center": v(-249.48, 200) * mm, "radius": 5 * mm});
            skCircle(sketch, "E13.2.21.0", {"center": v(-249.48, 225) * mm, "radius": 5 * mm});
            skCircle(sketch, "E13.2.22.0", {"center": v(-249.48, 250) * mm, "radius": 5 * mm});
            skCircle(sketch, "E13.2.23.0", {"center": v(-249.48, 275) * mm, "radius": 5 * mm});
            skCircle(sketch, "E13.2.24.0", {"center": v(-249.48, 300) * mm, "radius": 5 * mm});
            skCircle(sketch, "E13.3.0.0", {"center": v(-274.48, -300) * mm, "radius": 5 * mm});
            skCircle(sketch, "E13.3.1.0", {"center": v(-274.48, -275) * mm, "radius": 5 * mm});
            skCircle(sketch, "E13.3.2.0", {"center": v(-274.48, -250) * mm, "radius": 5 * mm});
            skCircle(sketch, "E13.3.3.0", {"center": v(-274.48, -225) * mm, "radius": 5 * mm});
            skCircle(sketch, "E13.3.4.0", {"center": v(-274.48, -200) * mm, "radius": 5 * mm});
            skCircle(sketch, "E13.3.5.0", {"center": v(-274.48, -175) * mm, "radius": 5 * mm});
            skCircle(sketch, "E13.3.6.0", {"center": v(-274.48, -150) * mm, "radius": 5 * mm});
            skCircle(sketch, "E13.3.7.0", {"center": v(-274.48, -125) * mm, "radius": 5 * mm});
            skCircle(sketch, "E13.3.8.0", {"center": v(-274.48, -100) * mm, "radius": 5 * mm});
            skCircle(sketch, "E13.3.9.0", {"center": v(-274.48, -75) * mm, "radius": 5 * mm});
            skCircle(sketch, "E13.3.10.0", {"center": v(-274.48, -50) * mm, "radius": 5 * mm});
            skCircle(sketch, "E13.3.11.0", {"center": v(-274.48, -25) * mm, "radius": 5 * mm});
            skCircle(sketch, "E13.3.12.0", {"center": v(-274.48, 0) * mm, "radius": 5 * mm});
            skCircle(sketch, "E13.3.13.0", {"center": v(-274.48, 25) * mm, "radius": 5 * mm});
            skCircle(sketch, "E13.3.14.0", {"center": v(-274.48, 50) * mm, "radius": 5 * mm});
            skCircle(sketch, "E13.3.15.0", {"center": v(-274.48, 75) * mm, "radius": 5 * mm});
            skCircle(sketch, "E13.3.16.0", {"center": v(-274.48, 100) * mm, "radius": 5 * mm});
            skCircle(sketch, "E13.3.17.0", {"center": v(-274.48, 125) * mm, "radius": 5 * mm});
            skCircle(sketch, "E13.3.18.0", {"center": v(-274.48, 150) * mm, "radius": 5 * mm});
            skCircle(sketch, "E13.3.19.0", {"center": v(-274.48, 175) * mm, "radius": 5 * mm});
            skCircle(sketch, "E13.3.20.0", {"center": v(-274.48, 200) * mm, "radius": 5 * mm});
            skCircle(sketch, "E13.3.21.0", {"center": v(-274.48, 225) * mm, "radius": 5 * mm});
            skCircle(sketch, "E13.3.22.0", {"center": v(-274.48, 250) * mm, "radius": 5 * mm});
            skCircle(sketch, "E13.3.23.0", {"center": v(-274.48, 275) * mm, "radius": 5 * mm});
            skCircle(sketch, "E13.3.24.0", {"center": v(-274.48, 300) * mm, "radius": 5 * mm});
            skCircle(sketch, "E13.4.0.0", {"center": v(-299.48, -300) * mm, "radius": 5 * mm});
            skCircle(sketch, "E13.4.1.0", {"center": v(-299.48, -275) * mm, "radius": 5 * mm});
            skCircle(sketch, "E13.4.2.0", {"center": v(-299.48, -250) * mm, "radius": 5 * mm});
            skCircle(sketch, "E13.4.3.0", {"center": v(-299.48, -225) * mm, "radius": 5 * mm});
            skCircle(sketch, "E13.4.4.0", {"center": v(-299.48, -200) * mm, "radius": 5 * mm});
            skCircle(sketch, "E13.4.5.0", {"center": v(-299.48, -175) * mm, "radius": 5 * mm});
            skCircle(sketch, "E13.4.6.0", {"center": v(-299.48, -150) * mm, "radius": 5 * mm});
            skCircle(sketch, "E13.4.7.0", {"center": v(-299.48, -125) * mm, "radius": 5 * mm});
            skCircle(sketch, "E13.4.8.0", {"center": v(-299.48, -100) * mm, "radius": 5 * mm});
            skCircle(sketch, "E13.4.9.0", {"center": v(-299.48, -75) * mm, "radius": 5 * mm});
            skCircle(sketch, "E13.4.10.0", {"center": v(-299.48, -50) * mm, "radius": 5 * mm});
            skCircle(sketch, "E13.4.11.0", {"center": v(-299.48, -25) * mm, "radius": 5 * mm});
            skCircle(sketch, "E13.4.12.0", {"center": v(-299.48, 0) * mm, "radius": 5 * mm});
            skCircle(sketch, "E13.4.13.0", {"center": v(-299.48, 25) * mm, "radius": 5 * mm});
            skCircle(sketch, "E13.4.14.0", {"center": v(-299.48, 50) * mm, "radius": 5 * mm});
            skCircle(sketch, "E13.4.15.0", {"center": v(-299.48, 75) * mm, "radius": 5 * mm});
            skCircle(sketch, "E13.4.16.0", {"center": v(-299.48, 100) * mm, "radius": 5 * mm});
            skCircle(sketch, "E13.4.17.0", {"center": v(-299.48, 125) * mm, "radius": 5 * mm});
            skCircle(sketch, "E13.4.18.0", {"center": v(-299.48, 150) * mm, "radius": 5 * mm});
            skCircle(sketch, "E13.4.19.0", {"center": v(-299.48, 175) * mm, "radius": 5 * mm});
            skCircle(sketch, "E13.4.20.0", {"center": v(-299.48, 200) * mm, "radius": 5 * mm});
            skCircle(sketch, "E13.4.21.0", {"center": v(-299.48, 225) * mm, "radius": 5 * mm});
            skCircle(sketch, "E13.4.22.0", {"center": v(-299.48, 250) * mm, "radius": 5 * mm});
            skCircle(sketch, "E13.4.23.0", {"center": v(-299.48, 275) * mm, "radius": 5 * mm});
            skCircle(sketch, "E13.4.24.0", {"center": v(-299.48, 300) * mm, "radius": 5 * mm});
            skCircle(sketch, "E13.5.0.0", {"center": v(-324.48, -300) * mm, "radius": 5 * mm});
            skCircle(sketch, "E13.5.1.0", {"center": v(-324.48, -275) * mm, "radius": 5 * mm});
            skCircle(sketch, "E13.5.2.0", {"center": v(-324.48, -250) * mm, "radius": 5 * mm});
            skCircle(sketch, "E13.5.3.0", {"center": v(-324.48, -225) * mm, "radius": 5 * mm});
            skCircle(sketch, "E13.5.4.0", {"center": v(-324.48, -200) * mm, "radius": 5 * mm});
            skCircle(sketch, "E13.5.5.0", {"center": v(-324.48, -175) * mm, "radius": 5 * mm});
            skCircle(sketch, "E13.5.6.0", {"center": v(-324.48, -150) * mm, "radius": 5 * mm});
            skCircle(sketch, "E13.5.7.0", {"center": v(-324.48, -125) * mm, "radius": 5 * mm});
            skCircle(sketch, "E13.5.8.0", {"center": v(-324.48, -100) * mm, "radius": 5 * mm});
            skCircle(sketch, "E13.5.9.0", {"center": v(-324.48, -75) * mm, "radius": 5 * mm});
            skCircle(sketch, "E13.5.10.0", {"center": v(-324.48, -50) * mm, "radius": 5 * mm});
            skCircle(sketch, "E13.5.11.0", {"center": v(-324.48, -25) * mm, "radius": 5 * mm});
            skCircle(sketch, "E13.5.12.0", {"center": v(-324.48, 0) * mm, "radius": 5 * mm});
            skCircle(sketch, "E13.5.13.0", {"center": v(-324.48, 25) * mm, "radius": 5 * mm});
            skCircle(sketch, "E13.5.14.0", {"center": v(-324.48, 50) * mm, "radius": 5 * mm});
            skCircle(sketch, "E13.5.15.0", {"center": v(-324.48, 75) * mm, "radius": 5 * mm});
            skCircle(sketch, "E13.5.16.0", {"center": v(-324.48, 100) * mm, "radius": 5 * mm});
            skCircle(sketch, "E13.5.17.0", {"center": v(-324.48, 125) * mm, "radius": 5 * mm});
            skCircle(sketch, "E13.5.18.0", {"center": v(-324.48, 150) * mm, "radius": 5 * mm});
            skCircle(sketch, "E13.5.19.0", {"center": v(-324.48, 175) * mm, "radius": 5 * mm});
            skCircle(sketch, "E13.5.20.0", {"center": v(-324.48, 200) * mm, "radius": 5 * mm});
            skCircle(sketch, "E13.5.21.0", {"center": v(-324.48, 225) * mm, "radius": 5 * mm});
            skCircle(sketch, "E13.5.22.0", {"center": v(-324.48, 250) * mm, "radius": 5 * mm});
            skCircle(sketch, "E13.5.23.0", {"center": v(-324.48, 275) * mm, "radius": 5 * mm});
            skCircle(sketch, "E13.5.24.0", {"center": v(-324.48, 300) * mm, "radius": 5 * mm});
            skCircle(sketch, "E13.6.0.0", {"center": v(-349.48, -300) * mm, "radius": 5 * mm});
            skCircle(sketch, "E13.6.1.0", {"center": v(-349.48, -275) * mm, "radius": 5 * mm});
            skCircle(sketch, "E13.6.2.0", {"center": v(-349.48, -250) * mm, "radius": 5 * mm});
            skCircle(sketch, "E13.6.3.0", {"center": v(-349.48, -225) * mm, "radius": 5 * mm});
            skCircle(sketch, "E13.6.4.0", {"center": v(-349.48, -200) * mm, "radius": 5 * mm});
            skCircle(sketch, "E13.6.5.0", {"center": v(-349.48, -175) * mm, "radius": 5 * mm});
            skCircle(sketch, "E13.6.6.0", {"center": v(-349.48, -150) * mm, "radius": 5 * mm});
            skCircle(sketch, "E13.6.7.0", {"center": v(-349.48, -125) * mm, "radius": 5 * mm});
            skCircle(sketch, "E13.6.8.0", {"center": v(-349.48, -100) * mm, "radius": 5 * mm});
            skCircle(sketch, "E13.6.9.0", {"center": v(-349.48, -75) * mm, "radius": 5 * mm});
            skCircle(sketch, "E13.6.10.0", {"center": v(-349.48, -50) * mm, "radius": 5 * mm});
            skCircle(sketch, "E13.6.11.0", {"center": v(-349.48, -25) * mm, "radius": 5 * mm});
            skCircle(sketch, "E13.6.12.0", {"center": v(-349.48, 0) * mm, "radius": 5 * mm});
            skCircle(sketch, "E13.6.13.0", {"center": v(-349.48, 25) * mm, "radius": 5 * mm});
            skCircle(sketch, "E13.6.14.0", {"center": v(-349.48, 50) * mm, "radius": 5 * mm});
            skCircle(sketch, "E13.6.15.0", {"center": v(-349.48, 75) * mm, "radius": 5 * mm});
            skCircle(sketch, "E13.6.16.0", {"center": v(-349.48, 100) * mm, "radius": 5 * mm});
            skCircle(sketch, "E13.6.17.0", {"center": v(-349.48, 125) * mm, "radius": 5 * mm});
            skCircle(sketch, "E13.6.18.0", {"center": v(-349.48, 150) * mm, "radius": 5 * mm});
            skCircle(sketch, "E13.6.19.0", {"center": v(-349.48, 175) * mm, "radius": 5 * mm});
            skCircle(sketch, "E13.6.20.0", {"center": v(-349.48, 200) * mm, "radius": 5 * mm});
            skCircle(sketch, "E13.6.21.0", {"center": v(-349.48, 225) * mm, "radius": 5 * mm});
            skCircle(sketch, "E13.6.22.0", {"center": v(-349.48, 250) * mm, "radius": 5 * mm});
            skCircle(sketch, "E13.6.23.0", {"center": v(-349.48, 275) * mm, "radius": 5 * mm});
            skCircle(sketch, "E13.6.24.0", {"center": v(-349.48, 300) * mm, "radius": 5 * mm});
            skCircle(sketch, "E13.7.0.0", {"center": v(-374.48, -300) * mm, "radius": 5 * mm});
            skCircle(sketch, "E13.7.1.0", {"center": v(-374.48, -275) * mm, "radius": 5 * mm});
            skCircle(sketch, "E13.7.2.0", {"center": v(-374.48, -250) * mm, "radius": 5 * mm});
            skCircle(sketch, "E13.7.3.0", {"center": v(-374.48, -225) * mm, "radius": 5 * mm});
            skCircle(sketch, "E13.7.4.0", {"center": v(-374.48, -200) * mm, "radius": 5 * mm});
            skCircle(sketch, "E13.7.5.0", {"center": v(-374.48, -175) * mm, "radius": 5 * mm});
            skCircle(sketch, "E13.7.6.0", {"center": v(-374.48, -150) * mm, "radius": 5 * mm});
            skCircle(sketch, "E13.7.7.0", {"center": v(-374.48, -125) * mm, "radius": 5 * mm});
            skCircle(sketch, "E13.7.8.0", {"center": v(-374.48, -100) * mm, "radius": 5 * mm});
            skCircle(sketch, "E13.7.9.0", {"center": v(-374.48, -75) * mm, "radius": 5 * mm});
            skCircle(sketch, "E13.7.10.0", {"center": v(-374.48, -50) * mm, "radius": 5 * mm});
            skCircle(sketch, "E13.7.11.0", {"center": v(-374.48, -25) * mm, "radius": 5 * mm});
            skCircle(sketch, "E13.7.12.0", {"center": v(-374.48, 0) * mm, "radius": 5 * mm});
            skCircle(sketch, "E13.7.13.0", {"center": v(-374.48, 25) * mm, "radius": 5 * mm});
            skCircle(sketch, "E13.7.14.0", {"center": v(-374.48, 50) * mm, "radius": 5 * mm});
            skCircle(sketch, "E13.7.15.0", {"center": v(-374.48, 75) * mm, "radius": 5 * mm});
            skCircle(sketch, "E13.7.16.0", {"center": v(-374.48, 100) * mm, "radius": 5 * mm});
            skCircle(sketch, "E13.7.17.0", {"center": v(-374.48, 125) * mm, "radius": 5 * mm});
            skCircle(sketch, "E13.7.18.0", {"center": v(-374.48, 150) * mm, "radius": 5 * mm});
            skCircle(sketch, "E13.7.19.0", {"center": v(-374.48, 175) * mm, "radius": 5 * mm});
            skCircle(sketch, "E13.7.20.0", {"center": v(-374.48, 200) * mm, "radius": 5 * mm});
            skCircle(sketch, "E13.7.21.0", {"center": v(-374.48, 225) * mm, "radius": 5 * mm});
            skCircle(sketch, "E13.7.22.0", {"center": v(-374.48, 250) * mm, "radius": 5 * mm});
            skCircle(sketch, "E13.7.23.0", {"center": v(-374.48, 275) * mm, "radius": 5 * mm});
            skCircle(sketch, "E13.7.24.0", {"center": v(-374.48, 300) * mm, "radius": 5 * mm});
            skCircle(sketch, "E13.8.0.0", {"center": v(-399.48, -300) * mm, "radius": 5 * mm});
            skCircle(sketch, "E13.8.1.0", {"center": v(-399.48, -275) * mm, "radius": 5 * mm});
            skCircle(sketch, "E13.8.2.0", {"center": v(-399.48, -250) * mm, "radius": 5 * mm});
            skCircle(sketch, "E13.8.3.0", {"center": v(-399.48, -225) * mm, "radius": 5 * mm});
            skCircle(sketch, "E13.8.4.0", {"center": v(-399.48, -200) * mm, "radius": 5 * mm});
            skCircle(sketch, "E13.8.5.0", {"center": v(-399.48, -175) * mm, "radius": 5 * mm});
            skCircle(sketch, "E13.8.6.0", {"center": v(-399.48, -150) * mm, "radius": 5 * mm});
            skCircle(sketch, "E13.8.7.0", {"center": v(-399.48, -125) * mm, "radius": 5 * mm});
            skCircle(sketch, "E13.8.8.0", {"center": v(-399.48, -100) * mm, "radius": 5 * mm});
            skCircle(sketch, "E13.8.9.0", {"center": v(-399.48, -75) * mm, "radius": 5 * mm});
            skCircle(sketch, "E13.8.10.0", {"center": v(-399.48, -50) * mm, "radius": 5 * mm});
            skCircle(sketch, "E13.8.11.0", {"center": v(-399.48, -25) * mm, "radius": 5 * mm});
            skCircle(sketch, "E13.8.12.0", {"center": v(-399.48, 0) * mm, "radius": 5 * mm});
            skCircle(sketch, "E13.8.13.0", {"center": v(-399.48, 25) * mm, "radius": 5 * mm});
            skCircle(sketch, "E13.8.14.0", {"center": v(-399.48, 50) * mm, "radius": 5 * mm});
            skCircle(sketch, "E13.8.15.0", {"center": v(-399.48, 75) * mm, "radius": 5 * mm});
            skCircle(sketch, "E13.8.16.0", {"center": v(-399.48, 100) * mm, "radius": 5 * mm});
            skCircle(sketch, "E13.8.17.0", {"center": v(-399.48, 125) * mm, "radius": 5 * mm});
            skCircle(sketch, "E13.8.18.0", {"center": v(-399.48, 150) * mm, "radius": 5 * mm});
            skCircle(sketch, "E13.8.19.0", {"center": v(-399.48, 175) * mm, "radius": 5 * mm});
            skCircle(sketch, "E13.8.20.0", {"center": v(-399.48, 200) * mm, "radius": 5 * mm});
            skCircle(sketch, "E13.8.21.0", {"center": v(-399.48, 225) * mm, "radius": 5 * mm});
            skCircle(sketch, "E13.8.22.0", {"center": v(-399.48, 250) * mm, "radius": 5 * mm});
            skCircle(sketch, "E13.8.23.0", {"center": v(-399.48, 275) * mm, "radius": 5 * mm});
            skCircle(sketch, "E13.8.24.0", {"center": v(-399.48, 300) * mm, "radius": 5 * mm});
            skCircle(sketch, "E13.9.0.0", {"center": v(-424.48, -300) * mm, "radius": 5 * mm});
            skCircle(sketch, "E13.9.1.0", {"center": v(-424.48, -275) * mm, "radius": 5 * mm});
            skCircle(sketch, "E13.9.2.0", {"center": v(-424.48, -250) * mm, "radius": 5 * mm});
            skCircle(sketch, "E13.9.3.0", {"center": v(-424.48, -225) * mm, "radius": 5 * mm});
            skCircle(sketch, "E13.9.4.0", {"center": v(-424.48, -200) * mm, "radius": 5 * mm});
            skCircle(sketch, "E13.9.5.0", {"center": v(-424.48, -175) * mm, "radius": 5 * mm});
            skCircle(sketch, "E13.9.6.0", {"center": v(-424.48, -150) * mm, "radius": 5 * mm});
            skCircle(sketch, "E13.9.7.0", {"center": v(-424.48, -125) * mm, "radius": 5 * mm});
            skCircle(sketch, "E13.9.8.0", {"center": v(-424.48, -100) * mm, "radius": 5 * mm});
            skCircle(sketch, "E13.9.9.0", {"center": v(-424.48, -75) * mm, "radius": 5 * mm});
            skCircle(sketch, "E13.9.10.0", {"center": v(-424.48, -50) * mm, "radius": 5 * mm});
            skCircle(sketch, "E13.9.11.0", {"center": v(-424.48, -25) * mm, "radius": 5 * mm});
            skCircle(sketch, "E13.9.12.0", {"center": v(-424.48, 0) * mm, "radius": 5 * mm});
            skCircle(sketch, "E13.9.13.0", {"center": v(-424.48, 25) * mm, "radius": 5 * mm});
            skCircle(sketch, "E13.9.14.0", {"center": v(-424.48, 50) * mm, "radius": 5 * mm});
            skCircle(sketch, "E13.9.15.0", {"center": v(-424.48, 75) * mm, "radius": 5 * mm});
            skCircle(sketch, "E13.9.16.0", {"center": v(-424.48, 100) * mm, "radius": 5 * mm});
            skCircle(sketch, "E13.9.17.0", {"center": v(-424.48, 125) * mm, "radius": 5 * mm});
            skCircle(sketch, "E13.9.18.0", {"center": v(-424.48, 150) * mm, "radius": 5 * mm});
            skCircle(sketch, "E13.9.19.0", {"center": v(-424.48, 175) * mm, "radius": 5 * mm});
            skCircle(sketch, "E13.9.20.0", {"center": v(-424.48, 200) * mm, "radius": 5 * mm});
            skCircle(sketch, "E13.9.21.0", {"center": v(-424.48, 225) * mm, "radius": 5 * mm});
            skCircle(sketch, "E13.9.22.0", {"center": v(-424.48, 250) * mm, "radius": 5 * mm});
            skCircle(sketch, "E13.9.23.0", {"center": v(-424.48, 275) * mm, "radius": 5 * mm});
            skCircle(sketch, "E13.9.24.0", {"center": v(-424.48, 300) * mm, "radius": 5 * mm});
            skCircle(sketch, "E13.10.0.0", {"center": v(-449.48, -300) * mm, "radius": 5 * mm});
            skCircle(sketch, "E13.10.1.0", {"center": v(-449.48, -275) * mm, "radius": 5 * mm});
            skCircle(sketch, "E13.10.2.0", {"center": v(-449.48, -250) * mm, "radius": 5 * mm});
            skCircle(sketch, "E13.10.3.0", {"center": v(-449.48, -225) * mm, "radius": 5 * mm});
            skCircle(sketch, "E13.10.4.0", {"center": v(-449.48, -200) * mm, "radius": 5 * mm});
            skCircle(sketch, "E13.10.5.0", {"center": v(-449.48, -175) * mm, "radius": 5 * mm});
            skCircle(sketch, "E13.10.6.0", {"center": v(-449.48, -150) * mm, "radius": 5 * mm});
            skCircle(sketch, "E13.10.7.0", {"center": v(-449.48, -125) * mm, "radius": 5 * mm});
            skCircle(sketch, "E13.10.8.0", {"center": v(-449.48, -100) * mm, "radius": 5 * mm});
            skCircle(sketch, "E13.10.9.0", {"center": v(-449.48, -75) * mm, "radius": 5 * mm});
            skCircle(sketch, "E13.10.10.0", {"center": v(-449.48, -50) * mm, "radius": 5 * mm});
            skCircle(sketch, "E13.10.11.0", {"center": v(-449.48, -25) * mm, "radius": 5 * mm});
            skCircle(sketch, "E13.10.12.0", {"center": v(-449.48, 0) * mm, "radius": 5 * mm});
            skCircle(sketch, "E13.10.13.0", {"center": v(-449.48, 25) * mm, "radius": 5 * mm});
            skCircle(sketch, "E13.10.14.0", {"center": v(-449.48, 50) * mm, "radius": 5 * mm});
            skCircle(sketch, "E13.10.15.0", {"center": v(-449.48, 75) * mm, "radius": 5 * mm});
            skCircle(sketch, "E13.10.16.0", {"center": v(-449.48, 100) * mm, "radius": 5 * mm});
            skCircle(sketch, "E13.10.17.0", {"center": v(-449.48, 125) * mm, "radius": 5 * mm});
            skCircle(sketch, "E13.10.18.0", {"center": v(-449.48, 150) * mm, "radius": 5 * mm});
            skCircle(sketch, "E13.10.19.0", {"center": v(-449.48, 175) * mm, "radius": 5 * mm});
            skCircle(sketch, "E13.10.20.0", {"center": v(-449.48, 200) * mm, "radius": 5 * mm});
            skCircle(sketch, "E13.10.21.0", {"center": v(-449.48, 225) * mm, "radius": 5 * mm});
            skCircle(sketch, "E13.10.22.0", {"center": v(-449.48, 250) * mm, "radius": 5 * mm});
            skCircle(sketch, "E13.10.23.0", {"center": v(-449.48, 275) * mm, "radius": 5 * mm});
            skCircle(sketch, "E13.10.24.0", {"center": v(-449.48, 300) * mm, "radius": 5 * mm});
            skSolve(sketch);
        }
        {
            var Q0;
            Q0 = qSketchRegion(id + "F4", true);
            extrude(context, id + "F5", {"entities" : qUnion([Q0]), "operationType" : NewBodyOperationType.REMOVE, "endBound" : BoundingType.THROUGH_ALL, "oppositeDirection" : true, "depth" : 25 * mm});
        }
        {
            var Q0;
            Q0=makeQuery(id+"F2.opShell","OFFSET_FACE",FACE,{"disambiguationData":[OSD([sQuery(id+"F0.wireOp",EDGE,"E0.top")])]});
            fillet(context, id + "F6", {"entities" : qUnion([Q0]), "radius" : 2.5 * mm, "tangentPropagation" : true, "allowEdgeOverflow" : false});
        }
    });
